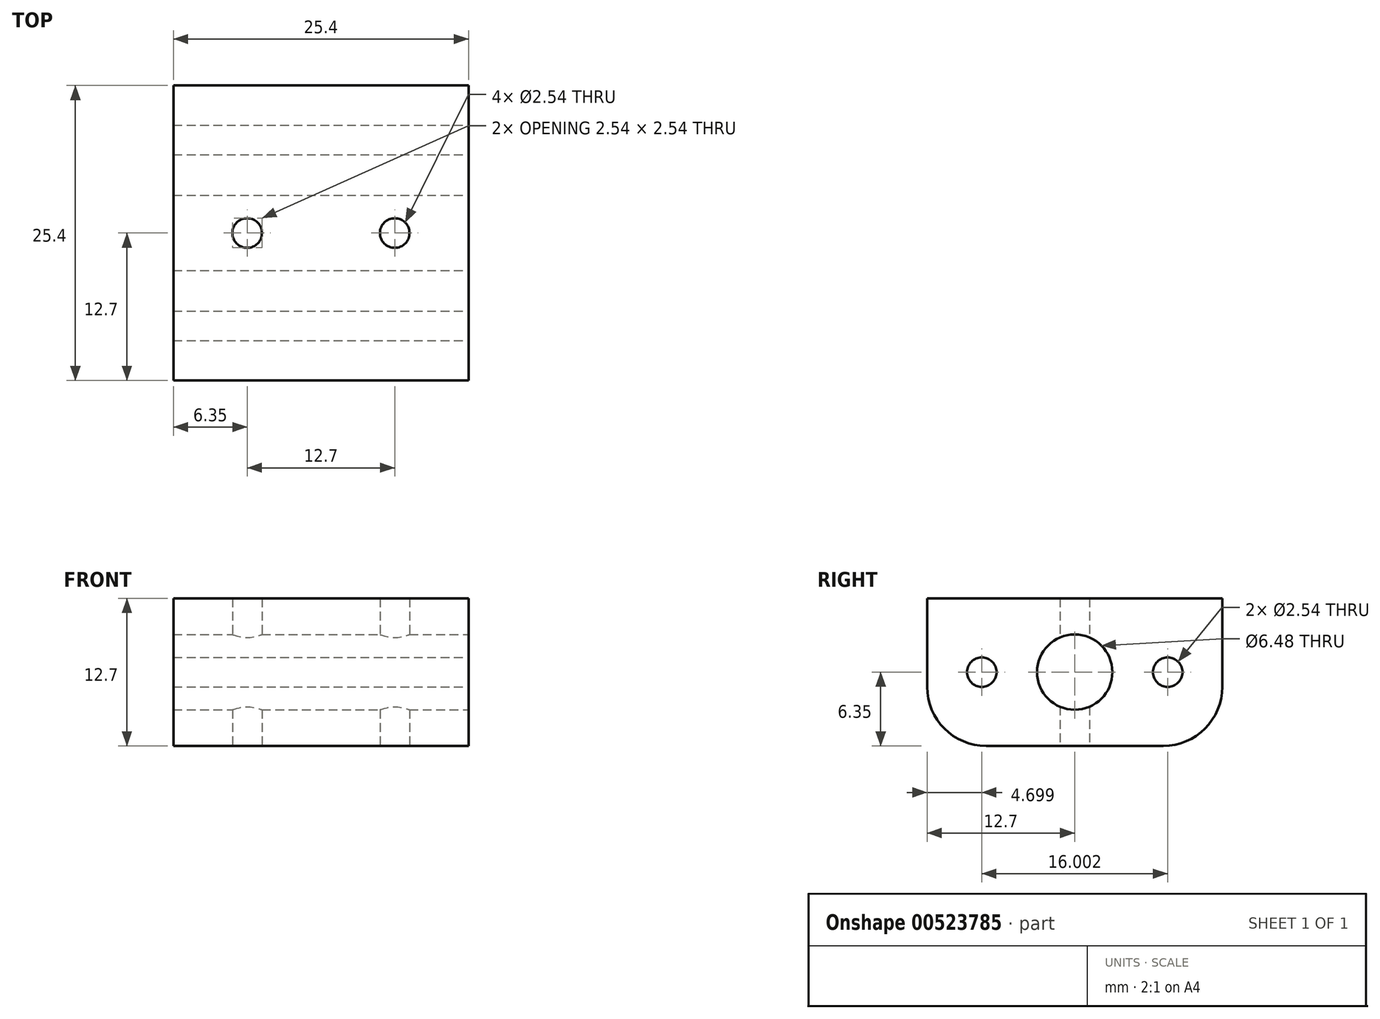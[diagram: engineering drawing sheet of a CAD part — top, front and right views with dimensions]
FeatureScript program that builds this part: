
annotation { "Feature Type Name" : "Feature", "Feature Type Description" : "" }
export const myFeature = defineFeature(function(context is Context, id is Id, definition is map)
    precondition{}
    {
        {
            var Q0;
            Q0=qCreatedBy(makeId("Top.planeOp"),FACE);
            var sketch = newSketch(context, id + "F0", { "sketchPlane" : qUnion([Q0])});
            skLineSegment(sketch, "E0.bottom", {"start": v(0, 0) * mm, "end": v(-25.4, 0) * mm});
            skLineSegment(sketch, "E0.top", {"start": v(0, 12.7) * mm, "end": v(-25.4, 12.7) * mm});
            skLineSegment(sketch, "E0.left", {"start": v(0, 0) * mm, "end": v(0, 12.7) * mm});
            skLineSegment(sketch, "E0.right", {"start": v(-25.4, 0) * mm, "end": v(-25.4, 12.7) * mm});
            skLineSegment(sketch, "E1", {"start": v(-12.7, 0) * mm, "end": v(-12.7, 6.35) * mm});
            skLineSegment(sketch, "E2", {"start": v(-12.7, 6.35) * mm, "end": v(-6.35, 6.35) * mm});
            skLineSegment(sketch, "E3", {"start": v(-6.35, 6.35) * mm, "end": v(-19.05, 6.35) * mm});
            skCircle(sketch, "E4", {"center": v(-6.35, 6.35) * mm, "radius": 1.27 * mm});
            skCircle(sketch, "E5", {"center": v(-19.05, 6.35) * mm, "radius": 1.27 * mm});
            skSolve(sketch);
        }
        {
            var Q0;
            Q0=makeQuery(id+"F0.imprint","IMPRINT",FACE,{"disambiguationData":[TD([[makeQuery(id+"F0.imprint","IMPRINT",EDGE,{"derivedFrom":sQuery(id+"F0.wireOp",EDGE,"E0.top")}),1.0]])]});
            extrude(context, id + "F1", {"entities" : qUnion([Q0]), "depth" : 12.7 * mm, "offsetDistance" : 25.4 * mm});
        }
        {
            var Q0;
            Q0=makeQuery(id+"F1.opExtrude","SWEPT_FACE",FACE,{"disambiguationData":[OSD([sQuery(id+"F0.wireOp",EDGE,"E0.bottom")])]});
            extrude(context, id + "F2", {"entities" : qUnion([Q0]), "operationType" : NewBodyOperationType.ADD, "depth" : 6.35 * mm, "offsetDistance" : 25.4 * mm});
        }
        {
            var Q0;
            Q0=makeQuery(id+"F1.opExtrude","SWEPT_FACE",FACE,{"disambiguationData":[OSD([sQuery(id+"F0.wireOp",EDGE,"E0.top")])]});
            extrude(context, id + "F3", {"entities" : qUnion([Q0]), "operationType" : NewBodyOperationType.ADD, "depth" : 6.35 * mm, "offsetDistance" : 25.4 * mm});
        }
        {
            var Q0;
            {var subQ0=sQuery(id+"F0.wireOp",EDGE,"E0.left");Q0=makeQuery(id+"F3.boolean.opBoolean","MERGE",FACE,{"derivedFrom":[makeQuery(id+"F2.boolean.opBoolean","MERGE",FACE,{"derivedFrom":[makeQuery(id+"F1.opExtrude","SWEPT_FACE",FACE,{"disambiguationData":[OSD([subQ0])]}),makeQuery(id+"F2.opExtrude","SWEPT_FACE",FACE,{"disambiguationData":[OSD([sQuery(id+"F0.wireOp",EDGE,"E0.bottom"),subQ0])]})]}),makeQuery(id+"F3.opExtrude","SWEPT_FACE",FACE,{"disambiguationData":[OSD([sQuery(id+"F0.wireOp",EDGE,"E0.top"),subQ0])]})]});}
            var sketch = newSketch(context, id + "F4", { "sketchPlane" : qUnion([Q0])});
            skLineSegment(sketch, "E6", {"start": v(6.35, 12.7) * mm, "end": v(6.35, 6.35) * mm});
            skLineSegment(sketch, "E7", {"start": v(6.35, 6.35) * mm, "end": v(14.35, 6.35) * mm});
            skLineSegment(sketch, "E8", {"start": v(6.35, 6.35) * mm, "end": v(-1.65, 6.35) * mm});
            skCircle(sketch, "E9", {"center": v(-1.65, 6.35) * mm, "radius": 1.27 * mm});
            skCircle(sketch, "E10", {"center": v(14.35, 6.35) * mm, "radius": 1.27 * mm});
            skCircle(sketch, "E11", {"center": v(6.35, 6.35) * mm, "radius": 3.24 * mm});
            skSolve(sketch);
        }
        {
            var Q0;
            Q0=makeQuery(id+"F4.imprint","IMPRINT",FACE,{"disambiguationData":[TD([[makeQuery(id+"F4.imprint","IMPRINT",EDGE,{"derivedFrom":sQuery(id+"F4.wireOp",EDGE,"E9")}),1.0]])]});
            var Q1;
            {var subQ1=sQuery(id+"F4.wireOp",EDGE,"E6");var subQ3=sQuery(id+"F4.wireOp",EDGE,"E11");var subQ4=makeQuery(id+"F4.imprint","INTERSECT",VERTEX,{"derivedFrom":[subQ1,subQ3]});Q1=makeQuery(id+"F4.imprint","IMPRINT",FACE,{"disambiguationData":[TD([[makeQuery(id+"F4.imprint","IMPRINT",EDGE,{"disambiguationData":[TD([[subQ4,-1.0]])],"derivedFrom":subQ3}),1.0]])]});}
            var Q2;
            {var subQ1=sQuery(id+"F4.wireOp",EDGE,"E6");var subQ3=sQuery(id+"F4.wireOp",EDGE,"E11");var subQ4=makeQuery(id+"F4.imprint","INTERSECT",VERTEX,{"derivedFrom":[subQ1,subQ3]});Q2=makeQuery(id+"F4.imprint","IMPRINT",FACE,{"disambiguationData":[TD([[makeQuery(id+"F4.imprint","IMPRINT",EDGE,{"disambiguationData":[TD([[subQ4,1.0]])],"derivedFrom":subQ3}),1.0]])]});}
            var Q3;
            {var subQ1=sQuery(id+"F4.wireOp",EDGE,"E7");var subQ3=sQuery(id+"F4.wireOp",EDGE,"E11");var subQ4=makeQuery(id+"F4.imprint","INTERSECT",VERTEX,{"derivedFrom":[subQ1,subQ3]});Q3=makeQuery(id+"F4.imprint","IMPRINT",FACE,{"disambiguationData":[TD([[makeQuery(id+"F4.imprint","IMPRINT",EDGE,{"disambiguationData":[TD([[subQ4,1.0]])],"derivedFrom":subQ3}),1.0]])]});}
            var Q4;
            Q4=makeQuery(id+"F4.imprint","IMPRINT",FACE,{"disambiguationData":[TD([[makeQuery(id+"F4.imprint","IMPRINT",EDGE,{"derivedFrom":sQuery(id+"F4.wireOp",EDGE,"E10")}),1.0]])]});
            extrude(context, id + "F5", {"entities" : qUnion([Q0, Q1, Q2, Q3, Q4]), "operationType" : NewBodyOperationType.REMOVE, "oppositeDirection" : true, "depth" : 50.8 * mm, "offsetDistance" : 25.4 * mm});
        }
        {
            var Q0;
            {var subQ0=sQuery(id+"F0.wireOp",EDGE,"E0.bottom");Q0=makeQuery(id+"F2.opExtrude","CAP_EDGE",EDGE,{"disambiguationData":[OSD([subQ0]),TDD([makeQuery(id+"F1.opExtrude","CAP_EDGE",EDGE,{"disambiguationData":[OSD([subQ0])],"isStart":true})])],"isStart":false});}
            var Q1;
            {var subQ0=sQuery(id+"F0.wireOp",EDGE,"E0.top");Q1=makeQuery(id+"F3.opExtrude","CAP_EDGE",EDGE,{"disambiguationData":[OSD([subQ0]),TDD([makeQuery(id+"F1.opExtrude","CAP_EDGE",EDGE,{"disambiguationData":[OSD([subQ0])],"isStart":true})])],"isStart":false});}
            fillet(context, id + "F6", {"entities" : qUnion([Q0, Q1]), "radius" : 5.08 * mm, "tangentPropagation" : true, "allowEdgeOverflow" : false});
        }
    });
